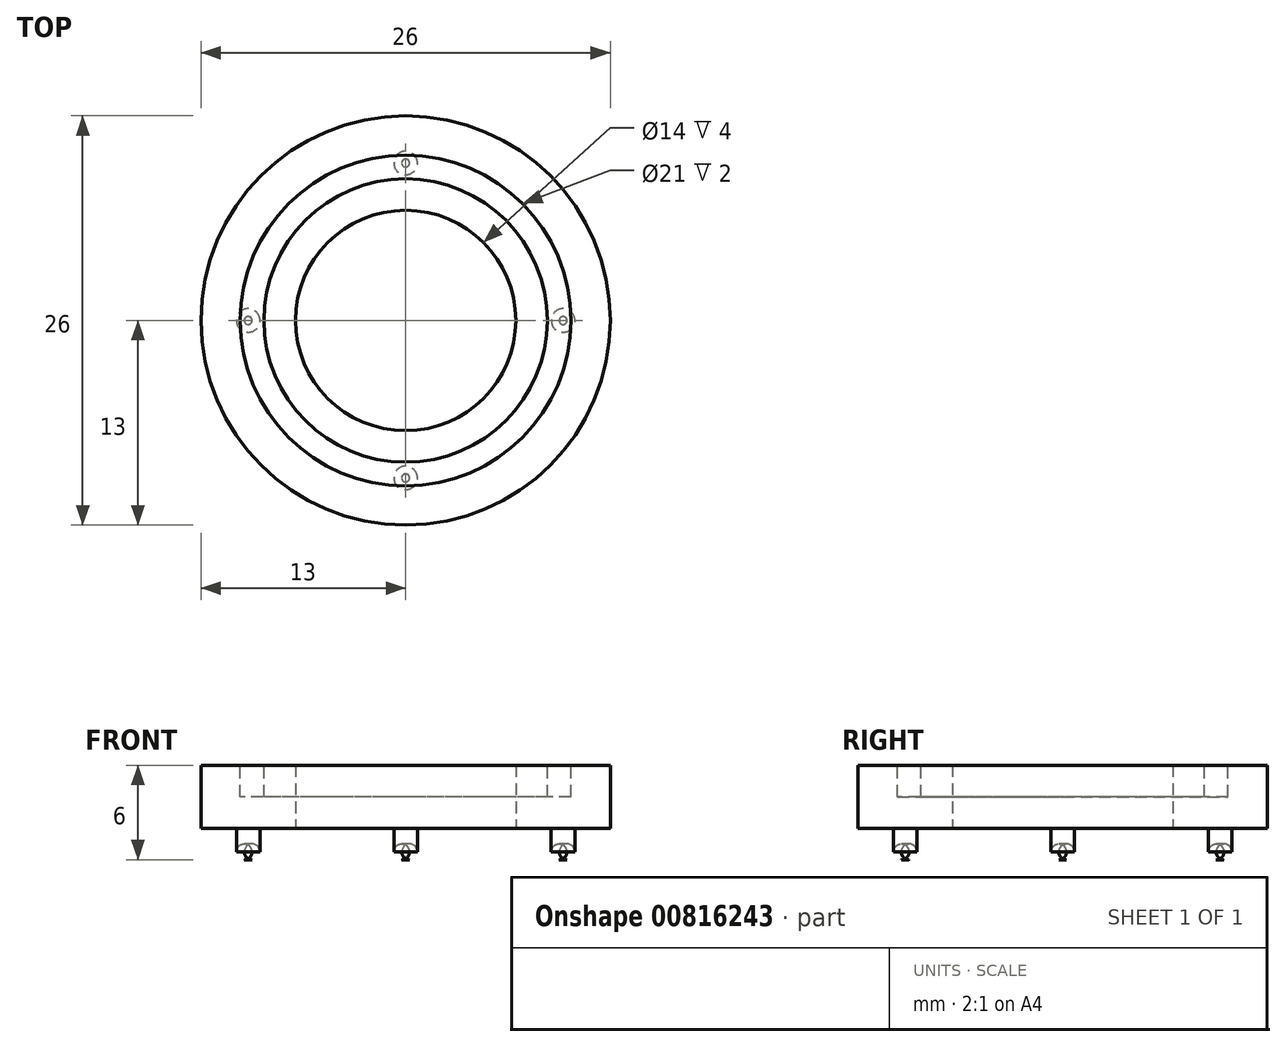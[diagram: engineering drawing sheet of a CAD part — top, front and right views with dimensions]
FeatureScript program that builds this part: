
annotation { "Feature Type Name" : "Feature", "Feature Type Description" : "" }
export const myFeature = defineFeature(function(context is Context, id is Id, definition is map)
    precondition{}
    {
        {
            var Q0;
            Q0=qCreatedBy(makeId("Top.planeOp"),FACE);
            var sketch = newSketch(context, id + "F0", { "sketchPlane" : qUnion([Q0])});
            skCircle(sketch, "E0", {"center": v(0, 0) * mm, "radius": 10 * mm, "construction": true});
            skCircle(sketch, "E1", {"center": v(0, 0) * mm, "radius": 7 * mm});
            skCircle(sketch, "E2", {"center": v(0, 0) * mm, "radius": 13 * mm});
            skSolve(sketch);
        }
        {
            var Q0;
            Q0=makeQuery(id+"F0.imprint","IMPRINT",FACE,{"disambiguationData":[TD([[makeQuery(id+"F0.imprint","IMPRINT",EDGE,{"derivedFrom":sQuery(id+"F0.wireOp",EDGE,"E1")}),-1.0]])]});
            extrude(context, id + "F1", {"entities" : qUnion([Q0]), "depth" : 4 * mm, "offsetDistance" : 25 * mm});
        }
        {
            var Q0;
            Q0=qCreatedBy(makeId("Top.planeOp"),FACE);
            var sketch = newSketch(context, id + "F2", { "sketchPlane" : qUnion([Q0])});
            skCircle(sketch, "E3", {"center": v(0, 0) * mm, "radius": 10 * mm, "construction": true});
            skPoint(sketch, "E4", {"position": v(0, -10) * mm});
            skCircle(sketch, "E5", {"center": v(0, -10) * mm, "radius": 0.75 * mm});
            skCircle(sketch, "E6.1.0", {"center": v(10, 0) * mm, "radius": 0.75 * mm});
            skCircle(sketch, "E6.2.0", {"center": v(0, 10) * mm, "radius": 0.75 * mm});
            skCircle(sketch, "E6.3.0", {"center": v(-10, 0) * mm, "radius": 0.75 * mm});
            skSolve(sketch);
        }
        {
            var Q0;
            Q0=makeQuery(id+"F2.imprint","IMPRINT",FACE,{"disambiguationData":[TD([[makeQuery(id+"F2.imprint","IMPRINT",EDGE,{"derivedFrom":sQuery(id+"F2.wireOp",EDGE,"E5")}),1.0]])]});
            var Q1;
            Q1=makeQuery(id+"F2.imprint","IMPRINT",FACE,{"disambiguationData":[TD([[makeQuery(id+"F2.imprint","IMPRINT",EDGE,{"derivedFrom":sQuery(id+"F2.wireOp",EDGE,"E6.3.0")}),1.0]])]});
            var Q2;
            Q2=makeQuery(id+"F2.imprint","IMPRINT",FACE,{"disambiguationData":[TD([[makeQuery(id+"F2.imprint","IMPRINT",EDGE,{"derivedFrom":sQuery(id+"F2.wireOp",EDGE,"E6.2.0")}),1.0]])]});
            var Q3;
            Q3=makeQuery(id+"F2.imprint","IMPRINT",FACE,{"disambiguationData":[TD([[makeQuery(id+"F2.imprint","IMPRINT",EDGE,{"derivedFrom":sQuery(id+"F2.wireOp",EDGE,"E6.1.0")}),1.0]])]});
            var Q4;
            Q4 = qConstructionFilter(qBodyType(qCreatedBy(id + "F2" ,EDGE), BodyType.WIRE), ConstructionObject.NO);
            extrude(context, id + "F3", {"entities" : qUnion([Q0, Q1, Q2, Q3]), "operationType" : NewBodyOperationType.ADD, "surfaceOperationType" : NewSurfaceOperationType.ADD, "surfaceEntities" : qUnion([Q4]), "oppositeDirection" : true, "depth" : 2 * mm, "offsetDistance" : 25 * mm});
        }
        {
            var Q0;
            Q0=makeQuery(id+"F3.opExtrude","CAP_EDGE",EDGE,{"disambiguationData":[OSD([sQuery(id+"F2.wireOp",EDGE,"E6.3.0")])],"isStart":false});
            var Q1;
            Q1=makeQuery(id+"F3.opExtrude","CAP_EDGE",EDGE,{"disambiguationData":[OSD([sQuery(id+"F2.wireOp",EDGE,"E5")])],"isStart":false});
            var Q2;
            Q2=makeQuery(id+"F3.opExtrude","CAP_EDGE",EDGE,{"disambiguationData":[OSD([sQuery(id+"F2.wireOp",EDGE,"E6.1.0")])],"isStart":false});
            var Q3;
            Q3=makeQuery(id+"F3.opExtrude","CAP_EDGE",EDGE,{"disambiguationData":[OSD([sQuery(id+"F2.wireOp",EDGE,"E6.2.0")])],"isStart":false});
            fillet(context, id + "F4", {"entities" : qUnion([Q0, Q1, Q2, Q3]), "radius" : 0.5 * mm, "allowEdgeOverflow" : false});
        }
        {
            var Q0;
            Q0=makeQuery(id+"F1.opExtrude","CAP_FACE",FACE,{"disambiguationData":[OSD([sQuery(id+"F0.wireOp",EDGE,"E1"),sQuery(id+"F0.wireOp",EDGE,"E2")])],"isStart":false});
            var sketch = newSketch(context, id + "F5", { "sketchPlane" : qUnion([Q0])});
            skCircle(sketch, "E7", {"center": v(0, 0) * mm, "radius": 9 * mm});
            skCircle(sketch, "E8", {"center": v(0, 0) * mm, "radius": 10.5 * mm});
            skSolve(sketch);
        }
        {
            var Q0;
            Q0 = qSketchRegion(id + "F5", true);
            extrude(context, id + "F6", {"entities" : qUnion([Q0]), "operationType" : NewBodyOperationType.REMOVE, "oppositeDirection" : true, "depth" : 2 * mm, "offsetDistance" : 25 * mm});
        }
    });
